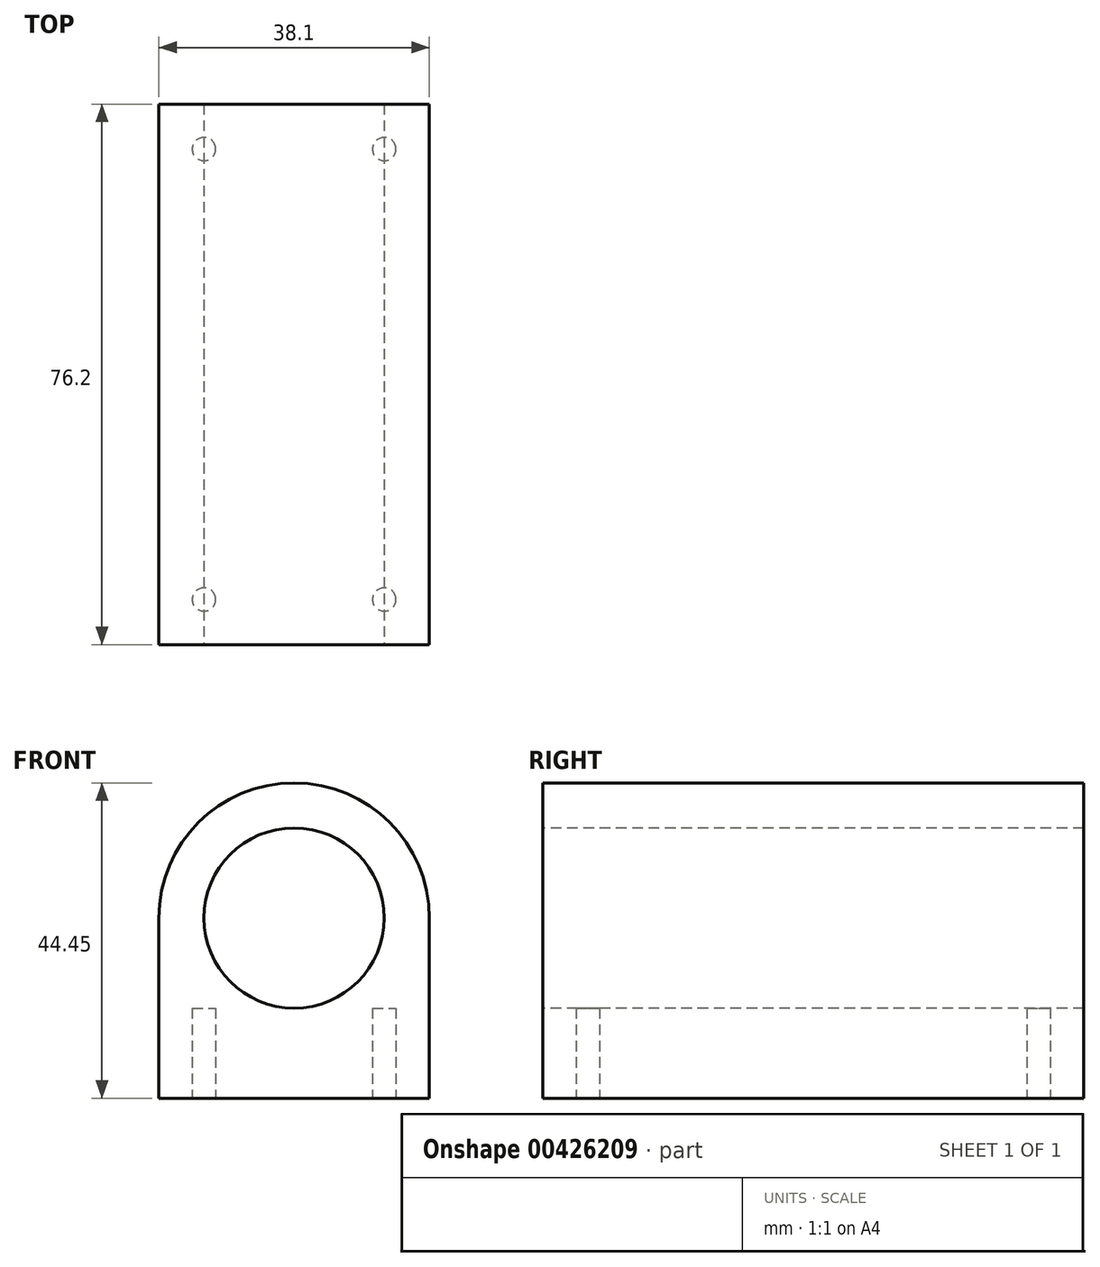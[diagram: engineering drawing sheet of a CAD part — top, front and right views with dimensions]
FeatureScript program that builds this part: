
annotation { "Feature Type Name" : "Feature", "Feature Type Description" : "" }
export const myFeature = defineFeature(function(context is Context, id is Id, definition is map)
    precondition{}
    {
        {
            var Q0;
            Q0=qCreatedBy(makeId("Front.planeOp"),FACE);
            var sketch = newSketch(context, id + "F0", { "sketchPlane" : qUnion([Q0])});
            skLineSegment(sketch, "E0.bottom", {"start": v(0, 0) * mm, "end": v(38.1, 0) * mm});
            skLineSegment(sketch, "E0.top", {"start": v(0, 44.45) * mm, "end": v(38.1, 44.45) * mm});
            skLineSegment(sketch, "E0.left", {"start": v(0, 0) * mm, "end": v(0, 44.45) * mm});
            skLineSegment(sketch, "E0.right", {"start": v(38.1, 0) * mm, "end": v(38.1, 44.45) * mm});
            skSolve(sketch);
        }
        {
            var Q0;
            Q0 = qSketchRegion(id + "F0", true);
            extrude(context, id + "F1", {"entities" : qUnion([Q0]), "depth" : 76.2 * mm});
        }
        {
            var Q0;
            Q0=makeQuery(id+"F1.opExtrude","SWEPT_EDGE",EDGE,{"disambiguationData":[OSD([sQuery(id+"F0.wireOp",EDGE,"E0.top"),sQuery(id+"F0.wireOp",EDGE,"E0.left")])]});
            var Q1;
            Q1=makeQuery(id+"F1.opExtrude","SWEPT_EDGE",EDGE,{"disambiguationData":[OSD([sQuery(id+"F0.wireOp",EDGE,"E0.top"),sQuery(id+"F0.wireOp",EDGE,"E0.right")])]});
            fillet(context, id + "F2", {"entities" : qUnion([Q0, Q1]), "radius" : 19.05 * mm, "tangentPropagation" : true, "allowEdgeOverflow" : false});
        }
        {
            var Q0;
            Q0=makeQuery(id+"F1.opExtrude","CAP_FACE",FACE,{"disambiguationData":[OSD([sQuery(id+"F0.wireOp",EDGE,"E0.bottom"),sQuery(id+"F0.wireOp",EDGE,"E0.top"),sQuery(id+"F0.wireOp",EDGE,"E0.left"),sQuery(id+"F0.wireOp",EDGE,"E0.right")])],"isStart":false});
            var sketch = newSketch(context, id + "F3", { "sketchPlane" : qUnion([Q0])});
            skCircle(sketch, "E1", {"center": v(19.05, 25.4) * mm, "radius": 12.7 * mm});
            skSolve(sketch);
        }
        {
            var Q0;
            Q0 = qSketchRegion(id + "F3", true);
            extrude(context, id + "F4", {"entities" : qUnion([Q0]), "operationType" : NewBodyOperationType.REMOVE, "endBound" : BoundingType.THROUGH_ALL, "oppositeDirection" : true, "depth" : 25.4 * mm});
        }
        {
            var Q0;
            Q0=makeQuery(id+"F1.opExtrude","SWEPT_FACE",FACE,{"disambiguationData":[OSD([sQuery(id+"F0.wireOp",EDGE,"E0.bottom")])]});
            var sketch = newSketch(context, id + "F5", { "sketchPlane" : qUnion([Q0])});
            skCircle(sketch, "E2", {"center": v(31.75, 69.85) * mm, "radius": 1.65 * mm});
            skCircle(sketch, "E3", {"center": v(6.35, 69.85) * mm, "radius": 1.65 * mm});
            skCircle(sketch, "E4", {"center": v(31.75, 6.35) * mm, "radius": 1.65 * mm});
            skCircle(sketch, "E5", {"center": v(6.35, 6.35) * mm, "radius": 1.65 * mm});
            skSolve(sketch);
        }
        {
            var Q0;
            Q0 = qSketchRegion(id + "F5", true);
            extrude(context, id + "F6", {"entities" : qUnion([Q0]), "operationType" : NewBodyOperationType.REMOVE, "oppositeDirection" : true, "depth" : 12.7 * mm});
        }
    });
